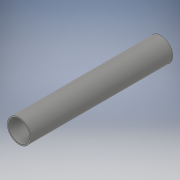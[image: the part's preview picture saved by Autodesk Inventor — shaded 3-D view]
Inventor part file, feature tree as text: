
AUTODESK INVENTOR PART (.ipt)
format: ipt  version: 2019 (Build 230136000, 136)  size: 97,792 bytes
history: native  units: mm
features: extrude x1, sketch x1
ambient origin geometry x8: Origin, YZ Plane, XZ Plane, XY Plane, X Axis, Y Axis, Z Axis, Center Point
bodies: Solide1 (feature_tree)
feature tree (2):
  extrude  "Extrusion1"  Depth=45.0mm
  sketch  "Esquisse1"
